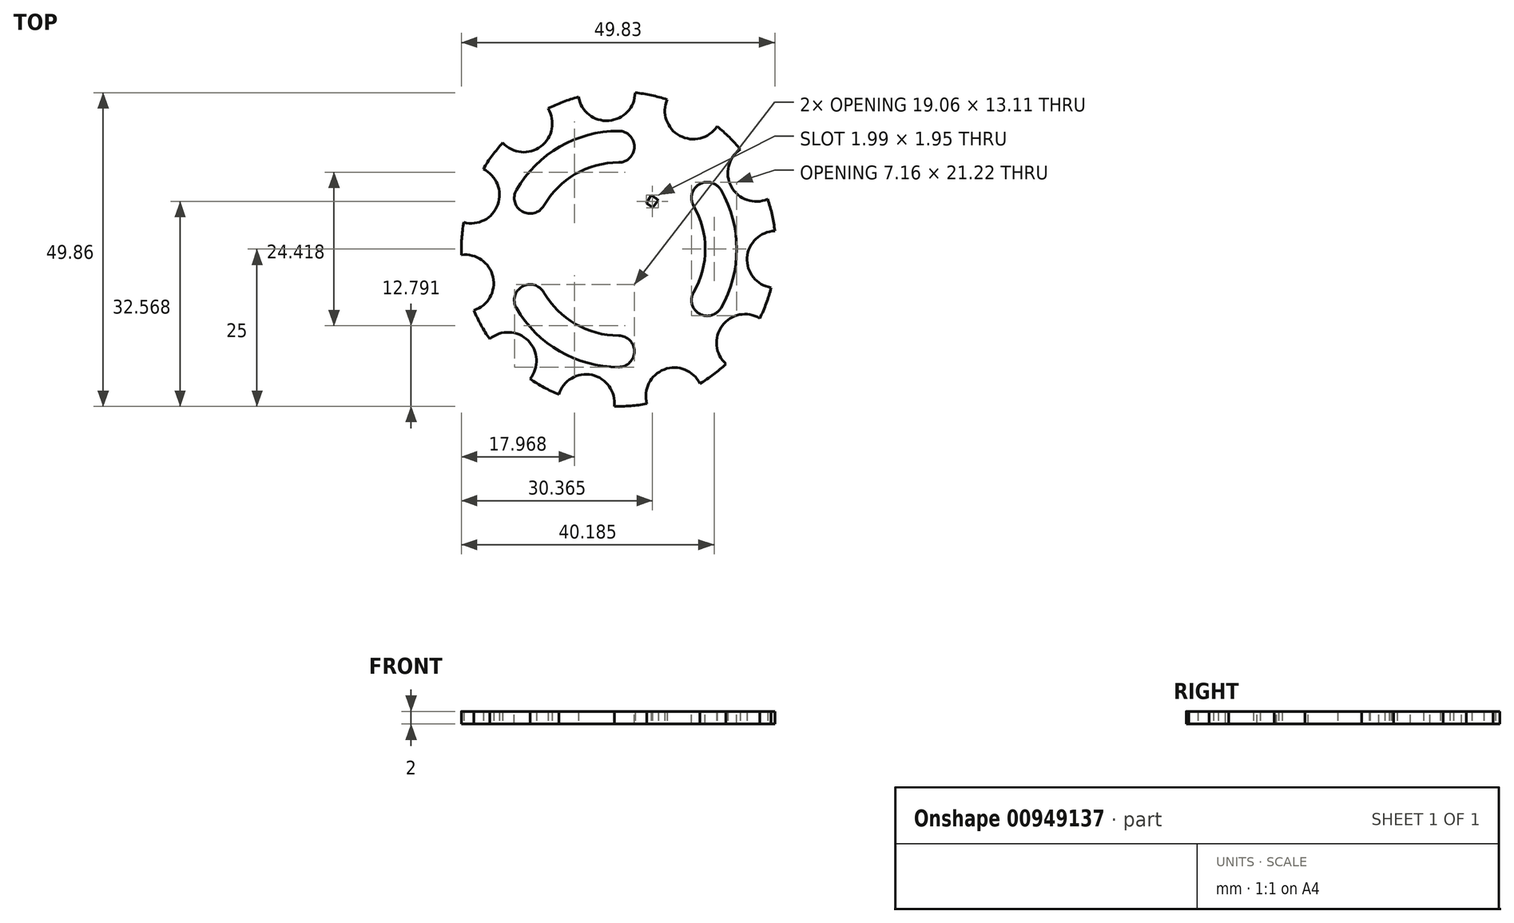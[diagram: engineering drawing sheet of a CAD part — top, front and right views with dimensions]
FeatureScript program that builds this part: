
annotation { "Feature Type Name" : "Feature", "Feature Type Description" : "" }
export const myFeature = defineFeature(function(context is Context, id is Id, definition is map)
    precondition{}
    {
        {
            var Q0;
            Q0=qCreatedBy(makeId("Top.planeOp"),FACE);
            var sketch = newSketch(context, id + "F0", { "sketchPlane" : qUnion([Q0])});
            skCircle(sketch, "E0", {"center": v(0, 0) * mm, "radius": 25 * mm});
            skCircle(sketch, "E1", {"center": v(0, 0) * mm, "radius": 10 * mm});
            skArc(sketch, "E2", {"start": v(4.39, 7.28) * mm, "mid": v(4.9, 6.94) * mm, "end": v(5.39, 6.57) * mm});
            skLineSegment(sketch, "E3", {"start": v(4.39, 7.28) * mm, "end": v(5.16, 8.56) * mm});
            skLineSegment(sketch, "E4", {"start": v(5.39, 6.57) * mm, "end": v(6.34, 7.73) * mm});
            skLineSegment(sketch, "E5.1.0", {"start": v(1.38, 8.39) * mm, "end": v(1.62, 9.87) * mm});
            skLineSegment(sketch, "E5.1.1", {"start": v(0.16, 8.5) * mm, "end": v(0.2, 10) * mm});
            skArc(sketch, "E5.1.2", {"start": v(0.16, 8.5) * mm, "mid": v(0.77, 8.46) * mm, "end": v(1.38, 8.39) * mm});
            skLineSegment(sketch, "E5.2.0", {"start": v(-3, 7.95) * mm, "end": v(-3.53, 9.36) * mm});
            skLineSegment(sketch, "E5.2.1", {"start": v(-4.1, 7.44) * mm, "end": v(-4.83, 8.75) * mm});
            skArc(sketch, "E5.2.2", {"start": v(-4.1, 7.44) * mm, "mid": v(-3.56, 7.72) * mm, "end": v(-3, 7.95) * mm});
            skLineSegment(sketch, "E5.3.0", {"start": v(-6.57, 5.39) * mm, "end": v(-7.73, 6.34) * mm});
            skLineSegment(sketch, "E5.3.1", {"start": v(-7.28, 4.39) * mm, "end": v(-8.56, 5.16) * mm});
            skArc(sketch, "E5.3.2", {"start": v(-7.28, 4.39) * mm, "mid": v(-6.94, 4.9) * mm, "end": v(-6.57, 5.39) * mm});
            skLineSegment(sketch, "E5.4.0", {"start": v(-8.39, 1.38) * mm, "end": v(-9.87, 1.62) * mm});
            skLineSegment(sketch, "E5.4.1", {"start": v(-8.5, 0.16) * mm, "end": v(-10, 0.2) * mm});
            skArc(sketch, "E5.4.2", {"start": v(-8.5, 0.16) * mm, "mid": v(-8.46, 0.77) * mm, "end": v(-8.39, 1.38) * mm});
            skLineSegment(sketch, "E5.5.0", {"start": v(-7.95, -3) * mm, "end": v(-9.36, -3.53) * mm});
            skLineSegment(sketch, "E5.5.1", {"start": v(-7.44, -4.1) * mm, "end": v(-8.75, -4.83) * mm});
            skArc(sketch, "E5.5.2", {"start": v(-7.44, -4.1) * mm, "mid": v(-7.72, -3.56) * mm, "end": v(-7.95, -3) * mm});
            skLineSegment(sketch, "E5.6.0", {"start": v(-5.39, -6.57) * mm, "end": v(-6.34, -7.73) * mm});
            skLineSegment(sketch, "E5.6.1", {"start": v(-4.39, -7.28) * mm, "end": v(-5.16, -8.56) * mm});
            skArc(sketch, "E5.6.2", {"start": v(-4.39, -7.28) * mm, "mid": v(-4.9, -6.94) * mm, "end": v(-5.39, -6.57) * mm});
            skLineSegment(sketch, "E5.7.0", {"start": v(-1.38, -8.39) * mm, "end": v(-1.62, -9.87) * mm});
            skLineSegment(sketch, "E5.7.1", {"start": v(-0.16, -8.5) * mm, "end": v(-0.2, -10) * mm});
            skArc(sketch, "E5.7.2", {"start": v(-0.16, -8.5) * mm, "mid": v(-0.77, -8.46) * mm, "end": v(-1.38, -8.39) * mm});
            skLineSegment(sketch, "E5.8.0", {"start": v(3, -7.95) * mm, "end": v(3.53, -9.36) * mm});
            skLineSegment(sketch, "E5.8.1", {"start": v(4.1, -7.44) * mm, "end": v(4.83, -8.75) * mm});
            skArc(sketch, "E5.8.2", {"start": v(4.1, -7.44) * mm, "mid": v(3.56, -7.72) * mm, "end": v(3, -7.95) * mm});
            skLineSegment(sketch, "E5.9.0", {"start": v(6.57, -5.39) * mm, "end": v(7.73, -6.34) * mm});
            skLineSegment(sketch, "E5.9.1", {"start": v(7.28, -4.39) * mm, "end": v(8.56, -5.16) * mm});
            skArc(sketch, "E5.9.2", {"start": v(7.28, -4.39) * mm, "mid": v(6.94, -4.9) * mm, "end": v(6.57, -5.39) * mm});
            skLineSegment(sketch, "E5.10.0", {"start": v(8.39, -1.38) * mm, "end": v(9.87, -1.62) * mm});
            skLineSegment(sketch, "E5.10.1", {"start": v(8.5, -0.16) * mm, "end": v(10, -0.2) * mm});
            skArc(sketch, "E5.10.2", {"start": v(8.5, -0.16) * mm, "mid": v(8.46, -0.77) * mm, "end": v(8.39, -1.38) * mm});
            skLineSegment(sketch, "E5.11.0", {"start": v(7.95, 3) * mm, "end": v(9.36, 3.53) * mm});
            skLineSegment(sketch, "E5.11.1", {"start": v(7.44, 4.1) * mm, "end": v(8.75, 4.83) * mm});
            skArc(sketch, "E5.11.2", {"start": v(7.44, 4.1) * mm, "mid": v(7.72, 3.56) * mm, "end": v(7.95, 3) * mm});
            skArc(sketch, "E6", {"start": v(-6.38, 24.17) * mm, "mid": v(-1.56, 20.4) * mm, "end": v(2.62, 24.86) * mm});
            skArc(sketch, "E7.1.0", {"start": v(-18.43, 16.89) * mm, "mid": v(-12.35, 16.32) * mm, "end": v(-11.23, 22.33) * mm});
            skArc(sketch, "E7.2.0", {"start": v(-24.64, 4.24) * mm, "mid": v(-19.21, 7.06) * mm, "end": v(-21.53, 12.71) * mm});
            skArc(sketch, "E7.3.0", {"start": v(-23.02, -9.75) * mm, "mid": v(-19.98, -4.45) * mm, "end": v(-24.98, -0.94) * mm});
            skArc(sketch, "E7.4.0", {"start": v(-14.1, -20.65) * mm, "mid": v(-14.4, -14.55) * mm, "end": v(-20.5, -14.3) * mm});
            skArc(sketch, "E7.5.0", {"start": v(-0.7, -25) * mm, "mid": v(-4.25, -20.02) * mm, "end": v(-9.52, -23.12) * mm});
            skArc(sketch, "E7.6.0", {"start": v(12.93, -21.4) * mm, "mid": v(7.25, -19.14) * mm, "end": v(4.49, -24.6) * mm});
            skArc(sketch, "E7.7.0", {"start": v(22.44, -11.01) * mm, "mid": v(16.45, -12.18) * mm, "end": v(17.07, -18.26) * mm});
            skArc(sketch, "E7.8.0", {"start": v(24.83, 2.87) * mm, "mid": v(20.42, -1.36) * mm, "end": v(24.24, -6.14) * mm});
            skArc(sketch, "E7.9.0", {"start": v(19.34, 15.84) * mm, "mid": v(17.92, 9.9) * mm, "end": v(23.7, 7.94) * mm});
            skArc(sketch, "E7.10.0", {"start": v(7.7, 23.78) * mm, "mid": v(9.72, 18.01) * mm, "end": v(15.65, 19.5) * mm});
            skSolve(sketch);
        }
        {
            var Q0;
            {var subQ16=sQuery(id+"F0.wireOp",EDGE,"E6");Q0=makeQuery(id+"F0.imprint","IMPRINT",FACE,{"disambiguationData":[TD([[makeQuery(id+"F0.imprint","IMPRINT",EDGE,{"derivedFrom":subQ16}),-1.0]])]});}
            extrude(context, id + "F1", {"entities" : qUnion([Q0]), "depth" : 2 * mm, "offsetDistance" : 25 * mm});
        }
        {
            var Q0;
            {var subQ0=sQuery(id+"F0.wireOp",EDGE,"E5.11.0");Q0=makeQuery(id+"F0.imprint","IMPRINT",FACE,{"disambiguationData":[TD([[makeQuery(id+"F0.imprint","IMPRINT",EDGE,{"derivedFrom":subQ0}),1.0]])]});}
            var Q1;
            Q1=makeQuery(id+"F0.imprint","IMPRINT",FACE,{"disambiguationData":[TD([[makeQuery(id+"F0.imprint","IMPRINT",EDGE,{"derivedFrom":sQuery(id+"F0.wireOp",EDGE,"E2")}),1.0]])]});
            var Q2;
            {var subQ0=sQuery(id+"F0.wireOp",EDGE,"E5.1.0");Q2=makeQuery(id+"F0.imprint","IMPRINT",FACE,{"disambiguationData":[TD([[makeQuery(id+"F0.imprint","IMPRINT",EDGE,{"derivedFrom":subQ0}),1.0]])]});}
            var Q3;
            {var subQ0=sQuery(id+"F0.wireOp",EDGE,"E5.10.0");Q3=makeQuery(id+"F0.imprint","IMPRINT",FACE,{"disambiguationData":[TD([[makeQuery(id+"F0.imprint","IMPRINT",EDGE,{"derivedFrom":subQ0}),1.0]])]});}
            var Q4;
            {var subQ0=sQuery(id+"F0.wireOp",EDGE,"E5.9.0");Q4=makeQuery(id+"F0.imprint","IMPRINT",FACE,{"disambiguationData":[TD([[makeQuery(id+"F0.imprint","IMPRINT",EDGE,{"derivedFrom":subQ0}),1.0]])]});}
            var Q5;
            {var subQ0=sQuery(id+"F0.wireOp",EDGE,"E5.8.0");Q5=makeQuery(id+"F0.imprint","IMPRINT",FACE,{"disambiguationData":[TD([[makeQuery(id+"F0.imprint","IMPRINT",EDGE,{"derivedFrom":subQ0}),1.0]])]});}
            var Q6;
            {var subQ0=sQuery(id+"F0.wireOp",EDGE,"E5.7.0");Q6=makeQuery(id+"F0.imprint","IMPRINT",FACE,{"disambiguationData":[TD([[makeQuery(id+"F0.imprint","IMPRINT",EDGE,{"derivedFrom":subQ0}),1.0]])]});}
            var Q7;
            {var subQ0=sQuery(id+"F0.wireOp",EDGE,"E5.6.0");Q7=makeQuery(id+"F0.imprint","IMPRINT",FACE,{"disambiguationData":[TD([[makeQuery(id+"F0.imprint","IMPRINT",EDGE,{"derivedFrom":subQ0}),1.0]])]});}
            var Q8;
            {var subQ0=sQuery(id+"F0.wireOp",EDGE,"E5.5.0");Q8=makeQuery(id+"F0.imprint","IMPRINT",FACE,{"disambiguationData":[TD([[makeQuery(id+"F0.imprint","IMPRINT",EDGE,{"derivedFrom":subQ0}),1.0]])]});}
            var Q9;
            {var subQ0=sQuery(id+"F0.wireOp",EDGE,"E5.4.0");Q9=makeQuery(id+"F0.imprint","IMPRINT",FACE,{"disambiguationData":[TD([[makeQuery(id+"F0.imprint","IMPRINT",EDGE,{"derivedFrom":subQ0}),1.0]])]});}
            var Q10;
            {var subQ0=sQuery(id+"F0.wireOp",EDGE,"E5.3.0");Q10=makeQuery(id+"F0.imprint","IMPRINT",FACE,{"disambiguationData":[TD([[makeQuery(id+"F0.imprint","IMPRINT",EDGE,{"derivedFrom":subQ0}),1.0]])]});}
            var Q11;
            {var subQ0=sQuery(id+"F0.wireOp",EDGE,"E5.2.0");Q11=makeQuery(id+"F0.imprint","IMPRINT",FACE,{"disambiguationData":[TD([[makeQuery(id+"F0.imprint","IMPRINT",EDGE,{"derivedFrom":subQ0}),1.0]])]});}
            extrude(context, id + "F2", {"entities" : qUnion([Q0, Q1, Q2, Q3, Q4, Q5, Q6, Q7, Q8, Q9, Q10, Q11]), "operationType" : NewBodyOperationType.ADD, "depth" : 2 * mm, "offsetDistance" : 25 * mm});
        }
        {
            var Q0;
            {var subQ0=sQuery(id+"F0.wireOp",EDGE,"E1");Q0=makeQuery(id+"F2.boolean.opBoolean","MERGE",FACE,{"derivedFrom":[makeQuery(id+"F1.opExtrude","CAP_FACE",FACE,{"disambiguationData":[OSD([sQuery(id+"F0.wireOp",EDGE,"E0"),subQ0,sQuery(id+"F0.wireOp",EDGE,"E6"),sQuery(id+"F0.wireOp",EDGE,"E7.1.0"),sQuery(id+"F0.wireOp",EDGE,"E7.2.0"),sQuery(id+"F0.wireOp",EDGE,"E7.3.0"),sQuery(id+"F0.wireOp",EDGE,"E7.4.0"),sQuery(id+"F0.wireOp",EDGE,"E7.5.0"),sQuery(id+"F0.wireOp",EDGE,"E7.6.0"),sQuery(id+"F0.wireOp",EDGE,"E7.7.0"),sQuery(id+"F0.wireOp",EDGE,"E7.8.0"),sQuery(id+"F0.wireOp",EDGE,"E7.9.0"),sQuery(id+"F0.wireOp",EDGE,"E7.10.0")])],"isStart":false}),makeQuery(id+"F2.opExtrude","CAP_FACE",FACE,{"disambiguationData":[OSD([subQ0,sQuery(id+"F0.wireOp",EDGE,"E5.11.0"),sQuery(id+"F0.wireOp",EDGE,"E5.11.1"),sQuery(id+"F0.wireOp",EDGE,"E5.11.2")])],"isStart":false}),makeQuery(id+"F2.opExtrude","CAP_FACE",FACE,{"disambiguationData":[OSD([subQ0,sQuery(id+"F0.wireOp",EDGE,"E2"),sQuery(id+"F0.wireOp",EDGE,"E3"),sQuery(id+"F0.wireOp",EDGE,"E4")])],"isStart":false}),makeQuery(id+"F2.opExtrude","CAP_FACE",FACE,{"disambiguationData":[OSD([subQ0,sQuery(id+"F0.wireOp",EDGE,"E5.1.0"),sQuery(id+"F0.wireOp",EDGE,"E5.1.1"),sQuery(id+"F0.wireOp",EDGE,"E5.1.2")])],"isStart":false}),makeQuery(id+"F2.opExtrude","CAP_FACE",FACE,{"disambiguationData":[OSD([subQ0,sQuery(id+"F0.wireOp",EDGE,"E5.2.0"),sQuery(id+"F0.wireOp",EDGE,"E5.2.1"),sQuery(id+"F0.wireOp",EDGE,"E5.2.2")])],"isStart":false}),makeQuery(id+"F2.opExtrude","CAP_FACE",FACE,{"disambiguationData":[OSD([subQ0,sQuery(id+"F0.wireOp",EDGE,"E5.3.0"),sQuery(id+"F0.wireOp",EDGE,"E5.3.1"),sQuery(id+"F0.wireOp",EDGE,"E5.3.2")])],"isStart":false}),makeQuery(id+"F2.opExtrude","CAP_FACE",FACE,{"disambiguationData":[OSD([subQ0,sQuery(id+"F0.wireOp",EDGE,"E5.4.0"),sQuery(id+"F0.wireOp",EDGE,"E5.4.1"),sQuery(id+"F0.wireOp",EDGE,"E5.4.2")])],"isStart":false}),makeQuery(id+"F2.opExtrude","CAP_FACE",FACE,{"disambiguationData":[OSD([subQ0,sQuery(id+"F0.wireOp",EDGE,"E5.5.0"),sQuery(id+"F0.wireOp",EDGE,"E5.5.1"),sQuery(id+"F0.wireOp",EDGE,"E5.5.2")])],"isStart":false}),makeQuery(id+"F2.opExtrude","CAP_FACE",FACE,{"disambiguationData":[OSD([subQ0,sQuery(id+"F0.wireOp",EDGE,"E5.6.0"),sQuery(id+"F0.wireOp",EDGE,"E5.6.1"),sQuery(id+"F0.wireOp",EDGE,"E5.6.2")])],"isStart":false}),makeQuery(id+"F2.opExtrude","CAP_FACE",FACE,{"disambiguationData":[OSD([subQ0,sQuery(id+"F0.wireOp",EDGE,"E5.7.0"),sQuery(id+"F0.wireOp",EDGE,"E5.7.1"),sQuery(id+"F0.wireOp",EDGE,"E5.7.2")])],"isStart":false}),makeQuery(id+"F2.opExtrude","CAP_FACE",FACE,{"disambiguationData":[OSD([subQ0,sQuery(id+"F0.wireOp",EDGE,"E5.8.0"),sQuery(id+"F0.wireOp",EDGE,"E5.8.1"),sQuery(id+"F0.wireOp",EDGE,"E5.8.2")])],"isStart":false}),makeQuery(id+"F2.opExtrude","CAP_FACE",FACE,{"disambiguationData":[OSD([subQ0,sQuery(id+"F0.wireOp",EDGE,"E5.9.0"),sQuery(id+"F0.wireOp",EDGE,"E5.9.1"),sQuery(id+"F0.wireOp",EDGE,"E5.9.2")])],"isStart":false}),makeQuery(id+"F2.opExtrude","CAP_FACE",FACE,{"disambiguationData":[OSD([subQ0,sQuery(id+"F0.wireOp",EDGE,"E5.10.0"),sQuery(id+"F0.wireOp",EDGE,"E5.10.1"),sQuery(id+"F0.wireOp",EDGE,"E5.10.2")])],"isStart":false})]});}
            var sketch = newSketch(context, id + "F3", { "sketchPlane" : qUnion([Q0])});
            skArc(sketch, "E8", {"start": v(0, 13.76) * mm, "mid": v(2.5, 16.26) * mm, "end": v(0, 18.76) * mm});
            skArc(sketch, "E9.1.0", {"start": v(-16.25, 9.38) * mm, "mid": v(-15.34, 5.97) * mm, "end": v(-11.92, 6.88) * mm});
            skArc(sketch, "E9.2.0", {"start": v(-11.92, -6.88) * mm, "mid": v(-15.34, -5.97) * mm, "end": v(-16.25, -9.38) * mm});
            skArc(sketch, "E9.3.0", {"start": v(0, -18.76) * mm, "mid": v(2.5, -16.26) * mm, "end": v(0, -13.76) * mm});
            skArc(sketch, "E9.4.0", {"start": v(11.92, -6.88) * mm, "mid": v(12.84, -10.3) * mm, "end": v(16.25, -9.38) * mm});
            skArc(sketch, "E9.5.0", {"start": v(16.25, 9.38) * mm, "mid": v(12.84, 10.3) * mm, "end": v(11.92, 6.88) * mm});
            skPoint(sketch, "E9.center", {"position": v(0, 0) * mm});
            skArc(sketch, "E10", {"start": v(0, 13.76) * mm, "mid": v(-6.88, 11.92) * mm, "end": v(-11.92, 6.88) * mm});
            skArc(sketch, "E11", {"start": v(0, 18.76) * mm, "mid": v(-9.38, 16.25) * mm, "end": v(-16.25, 9.38) * mm});
            skArc(sketch, "E12.trimOffspring", {"start": v(11.92, -6.88) * mm, "mid": v(13.76, 0) * mm, "end": v(11.92, 6.88) * mm});
            skArc(sketch, "E13.trimOffspring", {"start": v(16.25, -9.38) * mm, "mid": v(18.76, 0) * mm, "end": v(16.25, 9.38) * mm});
            skArc(sketch, "E14.trimOffspring", {"start": v(-11.92, -6.88) * mm, "mid": v(-6.88, -11.92) * mm, "end": v(0, -13.76) * mm});
            skArc(sketch, "E15.trimOffspring", {"start": v(-16.25, -9.38) * mm, "mid": v(-9.38, -16.25) * mm, "end": v(0, -18.76) * mm});
            skSolve(sketch);
        }
        {
            var Q0;
            Q0 = qSketchRegion(id + "F3", true);
            extrude(context, id + "F4", {"entities" : qUnion([Q0]), "operationType" : NewBodyOperationType.REMOVE, "oppositeDirection" : true, "depth" : 2 * mm, "offsetDistance" : 25 * mm});
        }
    });
